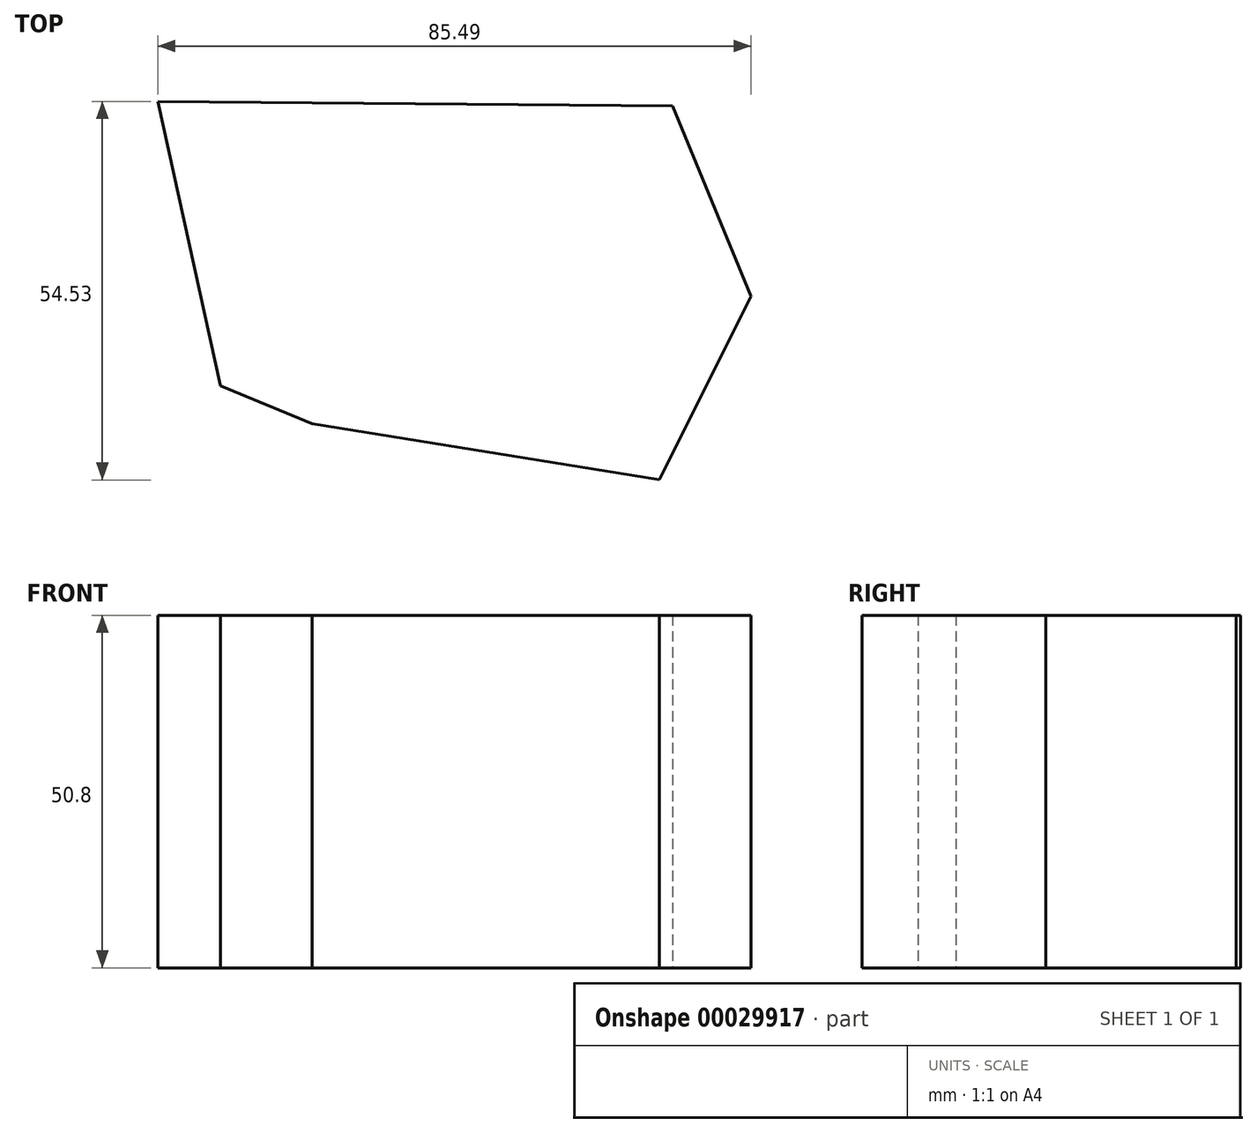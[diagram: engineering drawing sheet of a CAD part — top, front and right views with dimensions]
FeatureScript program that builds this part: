
annotation { "Feature Type Name" : "Feature", "Feature Type Description" : "" }
export const myFeature = defineFeature(function(context is Context, id is Id, definition is map)
    precondition{}
    {
        {
            var Q0;
            Q0=qCreatedBy(makeId("Top.planeOp"),FACE);
            var sketch = newSketch(context, id + "F0", { "sketchPlane" : qUnion([Q0])});
            skLineSegment(sketch, "E0", {"start": v(-37.42, 20.65) * mm, "end": v(-28.4, -20.33) * mm});
            skLineSegment(sketch, "E1", {"start": v(-28.4, -20.33) * mm, "end": v(-15.16, -25.8) * mm});
            skLineSegment(sketch, "E2", {"start": v(-15.16, -25.8) * mm, "end": v(34.84, -33.88) * mm});
            skLineSegment(sketch, "E3", {"start": v(34.84, -33.88) * mm, "end": v(48.07, -7.42) * mm});
            skLineSegment(sketch, "E4", {"start": v(48.07, -7.42) * mm, "end": v(36.78, 20) * mm});
            skLineSegment(sketch, "E5", {"start": v(36.78, 20) * mm, "end": v(-37.42, 20.65) * mm});
            skSolve(sketch);
        }
        {
            var Q0;
            Q0=makeQuery(id+"F0.imprint","IMPRINT",FACE,{"disambiguationData":[TD([[makeQuery(id+"F0.imprint","IMPRINT",EDGE,{"derivedFrom":sQuery(id+"F0.wireOp",EDGE,"E0")}),1.0]])]});
            extrude(context, id + "F1", {"entities" : qUnion([Q0]), "depth" : 50.8 * mm});
        }
        {
            var Q0;
            Q0=makeQuery(id+"F1.opExtrude","CAP_FACE",FACE,{"disambiguationData":[OSD([sQuery(id+"F0.wireOp",EDGE,"E0"),sQuery(id+"F0.wireOp",EDGE,"E1"),sQuery(id+"F0.wireOp",EDGE,"E2"),sQuery(id+"F0.wireOp",EDGE,"E3"),sQuery(id+"F0.wireOp",EDGE,"E4"),sQuery(id+"F0.wireOp",EDGE,"E5")])],"isStart":false});
            var sketch = newSketch(context, id + "F2", { "sketchPlane" : qUnion([Q0])});
            skLineSegment(sketch, "E6", {"start": v(-37.42, 20.65) * mm, "end": v(36.78, 20) * mm});
            skSolve(sketch);
        }
        {
            var Q0;
            Q0=sQuery(id+"F2.wireOp",EDGE,"E6");
            extrude(context, id + "F3", {"bodyType" : ToolBodyType.SURFACE, "surfaceEntities" : qUnion([Q0]), "depth" : 31.32 * mm});
        }
        {
            var Q0;
            Q0=makeQuery(id+"F3.opExtrude","SWEPT_FACE",FACE,{"disambiguationData":[OSD([sQuery(id+"F2.wireOp",EDGE,"E6")])]});
            var sketch = newSketch(context, id + "F4", { "sketchPlane" : qUnion([Q0])});
            skLineSegment(sketch, "E7", {"start": v(-37.6, 82.12) * mm, "end": v(36.6, 82.12) * mm});
            skSolve(sketch);
        }
        {
            var Q0;
            Q0=sQuery(id+"F4.wireOp",EDGE,"E7");
            extrude(context, id + "F5", {"bodyType" : ToolBodyType.SURFACE, "surfaceEntities" : qUnion([Q0]), "oppositeDirection" : true, "depth" : 44.76 * mm});
        }
    });
